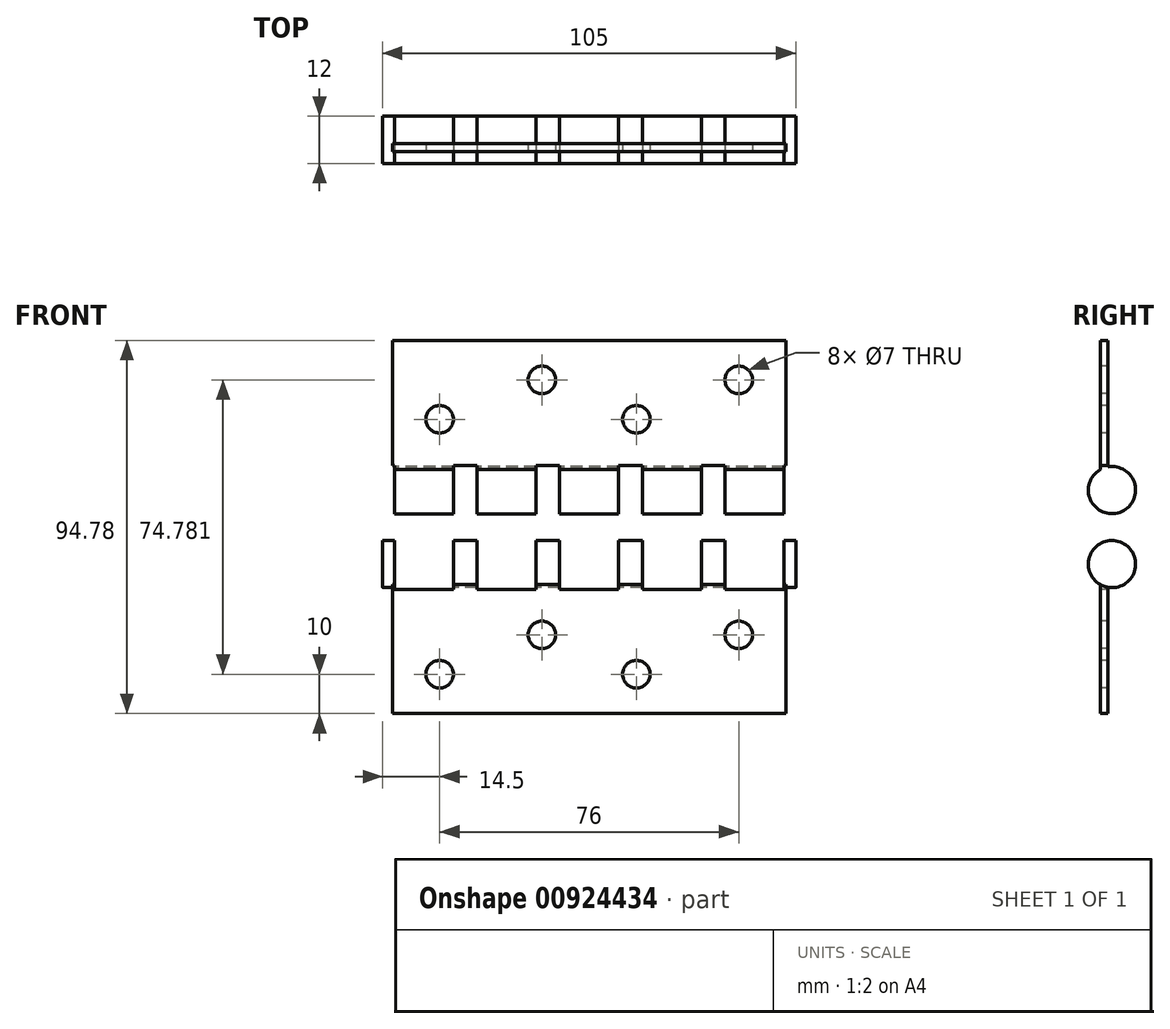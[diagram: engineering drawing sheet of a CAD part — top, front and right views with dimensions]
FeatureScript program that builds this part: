
annotation { "Feature Type Name" : "Feature", "Feature Type Description" : "" }
export const myFeature = defineFeature(function(context is Context, id is Id, definition is map)
    precondition{}
    {
        {
            var Q0;
            Q0=qCreatedBy(makeId("Right.planeOp"),FACE);
            var sketch = newSketch(context, id + "F0", { "sketchPlane" : qUnion([Q0])});
            skArc(sketch, "E0", {"start": v(-1, 32.08) * mm, "mid": v(2.03, 43.65) * mm, "end": v(-3, 32.8) * mm});
            skLineSegment(sketch, "E1", {"start": v(-1, 32.08) * mm, "end": v(-1, 0) * mm});
            skLineSegment(sketch, "E2", {"start": v(-1, 0) * mm, "end": v(-3, 0) * mm});
            skLineSegment(sketch, "E3", {"start": v(-3, 0) * mm, "end": v(-3, 32.8) * mm});
            skSolve(sketch);
        }
        {
            var Q0;
            Q0 = qSketchRegion(id + "F0", true);
            extrude(context, id + "F1", {"entities" : qUnion([Q0]), "depth" : 100 * mm, "offsetDistance" : 25 * mm});
        }
        {
            var Q0;
            Q0=makeQuery(id+"F1.opExtrude","CAP_FACE",FACE,{"disambiguationData":[OSD([sQuery(id+"F0.wireOp",EDGE,"NNvxePe8-nNrL-2dZQ-cABt-9JlAzgXYuufM.bottom"),sQuery(id+"F0.wireOp",EDGE,"NNvxePe8-nNrL-2dZQ-cABt-9JlAzgXYuufM.left"),sQuery(id+"F0.wireOp",EDGE,"NNvxePe8-nNrL-2dZQ-cABt-9JlAzgXYuufM.right"),sQuery(id+"F0.wireOp",EDGE,"E0")])],"isStart":false});
            var sketch = newSketch(context, id + "F2", { "sketchPlane" : qUnion([Q0])});
            skCircle(sketch, "E4", {"center": v(0, 38) * mm, "radius": 6 * mm});
            skSolve(sketch);
        }
        {
            var Q0;
            Q0 = qSketchRegion(id + "F2", true);
            extrude(context, id + "F3", {"entities" : qUnion([Q0]), "operationType" : NewBodyOperationType.ADD, "depth" : 2.5 * mm, "offsetDistance" : 25 * mm});
        }
        {
            var Q0;
            Q0=makeQuery(id+"F1.opExtrude","CAP_FACE",FACE,{"disambiguationData":[OSD([sQuery(id+"F0.wireOp",EDGE,"NNvxePe8-nNrL-2dZQ-cABt-9JlAzgXYuufM.bottom"),sQuery(id+"F0.wireOp",EDGE,"NNvxePe8-nNrL-2dZQ-cABt-9JlAzgXYuufM.left"),sQuery(id+"F0.wireOp",EDGE,"NNvxePe8-nNrL-2dZQ-cABt-9JlAzgXYuufM.right"),sQuery(id+"F0.wireOp",EDGE,"E0")])],"isStart":true});
            var sketch = newSketch(context, id + "F4", { "sketchPlane" : qUnion([Q0])});
            skCircle(sketch, "E5", {"center": v(0, 38) * mm, "radius": 6 * mm});
            skSolve(sketch);
        }
        {
            var Q0;
            Q0 = qSketchRegion(id + "F4", true);
            extrude(context, id + "F5", {"entities" : qUnion([Q0]), "operationType" : NewBodyOperationType.ADD, "depth" : 2.5 * mm, "offsetDistance" : 25 * mm});
        }
        {
            var Q0;
            Q0=makeQuery(id+"F1.opExtrude","CAP_FACE",FACE,{"disambiguationData":[OSD([sQuery(id+"F0.wireOp",EDGE,"NNvxePe8-nNrL-2dZQ-cABt-9JlAzgXYuufM.bottom"),sQuery(id+"F0.wireOp",EDGE,"NNvxePe8-nNrL-2dZQ-cABt-9JlAzgXYuufM.left"),sQuery(id+"F0.wireOp",EDGE,"NNvxePe8-nNrL-2dZQ-cABt-9JlAzgXYuufM.right"),sQuery(id+"F0.wireOp",EDGE,"E0")])],"isStart":true});
            var sketch = newSketch(context, id + "F6", { "sketchPlane" : qUnion([Q0])});
            skLineSegment(sketch, "E6.bottom", {"start": v(1, 94.78) * mm, "end": v(3, 94.78) * mm});
            skLineSegment(sketch, "E6.left", {"start": v(1, 94.78) * mm, "end": v(1, 62.7) * mm});
            skLineSegment(sketch, "E6.right", {"start": v(3, 94.78) * mm, "end": v(3, 61.98) * mm});
            skArc(sketch, "E7", {"start": v(1, 62.7) * mm, "mid": v(-2.03, 51.14) * mm, "end": v(3, 61.98) * mm});
            skSolve(sketch);
        }
        {
            var Q0;
            Q0=makeQuery(id+"F6.imprint","IMPRINT",FACE,{"disambiguationData":[TD([[makeQuery(id+"F6.imprint","IMPRINT",EDGE,{"derivedFrom":sQuery(id+"F6.wireOp",EDGE,"E6.bottom")}),-1.0]])]});
            extrude(context, id + "F7", {"entities" : qUnion([Q0]), "oppositeDirection" : true, "depth" : 100 * mm, "offsetDistance" : 25 * mm});
        }
        {
            var Q0;
            Q0=makeQuery(id+"F1.opExtrude","SWEPT_FACE",FACE,{"disambiguationData":[OSD([sQuery(id+"F0.wireOp",EDGE,"E3")])]});
            var sketch = newSketch(context, id + "F8", { "sketchPlane" : qUnion([Q0])});
            skLineSegment(sketch, "E8.bottom", {"start": v(0.5, 46.58) * mm, "end": v(15.5, 46.58) * mm});
            skLineSegment(sketch, "E8.top", {"start": v(0, 31.58) * mm, "end": v(15.5, 31.58) * mm});
            skLineSegment(sketch, "E8.left", {"start": v(0.5, 46.58) * mm, "end": v(0.5, 31.58) * mm});
            skLineSegment(sketch, "E8.right", {"start": v(15.5, 46.58) * mm, "end": v(15.5, 31.58) * mm});
            skLineSegment(sketch, "E9.1.0.0", {"start": v(36.5, 46.58) * mm, "end": v(36.5, 31.58) * mm});
            skLineSegment(sketch, "E9.1.0.1", {"start": v(21, 31.58) * mm, "end": v(36.5, 31.58) * mm});
            skLineSegment(sketch, "E9.1.0.2", {"start": v(21.5, 46.58) * mm, "end": v(36.5, 46.58) * mm});
            skLineSegment(sketch, "E9.1.0.3", {"start": v(21.5, 46.58) * mm, "end": v(21.5, 31.58) * mm});
            skLineSegment(sketch, "E9.2.0.0", {"start": v(57.5, 46.58) * mm, "end": v(57.5, 31.58) * mm});
            skLineSegment(sketch, "E9.2.0.1", {"start": v(42, 31.58) * mm, "end": v(57.5, 31.58) * mm});
            skLineSegment(sketch, "E9.2.0.2", {"start": v(42.5, 46.58) * mm, "end": v(57.5, 46.58) * mm});
            skLineSegment(sketch, "E9.2.0.3", {"start": v(42.5, 46.58) * mm, "end": v(42.5, 31.58) * mm});
            skLineSegment(sketch, "E9.3.0.0", {"start": v(78.5, 46.58) * mm, "end": v(78.5, 31.58) * mm});
            skLineSegment(sketch, "E9.3.0.1", {"start": v(63, 31.58) * mm, "end": v(78.5, 31.58) * mm});
            skLineSegment(sketch, "E9.3.0.2", {"start": v(63.5, 46.58) * mm, "end": v(78.5, 46.58) * mm});
            skLineSegment(sketch, "E9.3.0.3", {"start": v(63.5, 46.58) * mm, "end": v(63.5, 31.58) * mm});
            skLineSegment(sketch, "E9.4.0.0", {"start": v(99.5, 46.58) * mm, "end": v(99.5, 31.58) * mm});
            skLineSegment(sketch, "E9.4.0.1", {"start": v(84, 31.58) * mm, "end": v(99.5, 31.58) * mm});
            skLineSegment(sketch, "E9.4.0.2", {"start": v(84.5, 46.58) * mm, "end": v(99.5, 46.58) * mm});
            skLineSegment(sketch, "E9.4.0.3", {"start": v(84.5, 46.58) * mm, "end": v(84.5, 31.58) * mm});
            skLineSegment(sketch, "E9.direction1", {"start": v(0, 31.58) * mm, "end": v(21, 31.58) * mm, "construction": true});
            skSolve(sketch);
        }
        {
            var Q0;
            Q0 = qSketchRegion(id + "F8", true);
            extrude(context, id + "F9", {"entities" : qUnion([Q0]), "operationType" : NewBodyOperationType.REMOVE, "oppositeDirection" : true, "depth" : 25 * mm, "offsetDistance" : 25 * mm, "hasSecondDirection" : true, "secondDirectionOppositeDirection" : false, "secondDirectionDepth" : 25 * mm});
        }
        {
            var Q0;
            Q0=makeQuery(id+"F7.opExtrude","SWEPT_FACE",FACE,{"disambiguationData":[OSD([sQuery(id+"F6.wireOp",EDGE,"E6.right")])]});
            var sketch = newSketch(context, id + "F10", { "sketchPlane" : qUnion([Q0])});
            skLineSegment(sketch, "E10.bottom", {"start": v(-5.5, 62.98) * mm, "end": v(0.5, 62.98) * mm});
            skLineSegment(sketch, "E10.top", {"start": v(-5.5, 46.98) * mm, "end": v(0.5, 46.98) * mm});
            skLineSegment(sketch, "E10.left", {"start": v(-5.5, 62.98) * mm, "end": v(-5.5, 46.98) * mm});
            skLineSegment(sketch, "E10.right", {"start": v(0.5, 62.98) * mm, "end": v(0.5, 46.98) * mm});
            skLineSegment(sketch, "E11.1.0.0", {"start": v(15.5, 46.98) * mm, "end": v(21.5, 46.98) * mm});
            skLineSegment(sketch, "E11.1.0.1", {"start": v(21.5, 62.98) * mm, "end": v(21.5, 46.98) * mm});
            skLineSegment(sketch, "E11.1.0.2", {"start": v(15.5, 62.98) * mm, "end": v(15.5, 46.98) * mm});
            skLineSegment(sketch, "E11.1.0.3", {"start": v(15.5, 62.98) * mm, "end": v(21.5, 62.98) * mm});
            skLineSegment(sketch, "E11.2.0.0", {"start": v(36.5, 46.98) * mm, "end": v(42.5, 46.98) * mm});
            skLineSegment(sketch, "E11.2.0.1", {"start": v(42.5, 62.98) * mm, "end": v(42.5, 46.98) * mm});
            skLineSegment(sketch, "E11.2.0.2", {"start": v(36.5, 62.98) * mm, "end": v(36.5, 46.98) * mm});
            skLineSegment(sketch, "E11.2.0.3", {"start": v(36.5, 62.98) * mm, "end": v(42.5, 62.98) * mm});
            skLineSegment(sketch, "E11.3.0.0", {"start": v(57.5, 46.98) * mm, "end": v(63.5, 46.98) * mm});
            skLineSegment(sketch, "E11.3.0.1", {"start": v(63.5, 62.98) * mm, "end": v(63.5, 46.98) * mm});
            skLineSegment(sketch, "E11.3.0.2", {"start": v(57.5, 62.98) * mm, "end": v(57.5, 46.98) * mm});
            skLineSegment(sketch, "E11.3.0.3", {"start": v(57.5, 62.98) * mm, "end": v(63.5, 62.98) * mm});
            skLineSegment(sketch, "E11.4.0.0", {"start": v(78.5, 46.98) * mm, "end": v(84.5, 46.98) * mm});
            skLineSegment(sketch, "E11.4.0.1", {"start": v(84.5, 62.98) * mm, "end": v(84.5, 46.98) * mm});
            skLineSegment(sketch, "E11.4.0.2", {"start": v(78.5, 62.98) * mm, "end": v(78.5, 46.98) * mm});
            skLineSegment(sketch, "E11.4.0.3", {"start": v(78.5, 62.98) * mm, "end": v(84.5, 62.98) * mm});
            skLineSegment(sketch, "E11.5.0.0", {"start": v(99.5, 46.98) * mm, "end": v(105.5, 46.98) * mm});
            skLineSegment(sketch, "E11.5.0.1", {"start": v(105.5, 62.98) * mm, "end": v(105.5, 46.98) * mm});
            skLineSegment(sketch, "E11.5.0.2", {"start": v(99.5, 62.98) * mm, "end": v(99.5, 46.98) * mm});
            skLineSegment(sketch, "E11.5.0.3", {"start": v(99.5, 62.98) * mm, "end": v(105.5, 62.98) * mm});
            skLineSegment(sketch, "E11.direction1", {"start": v(-5.5, 46.98) * mm, "end": v(15.5, 46.98) * mm, "construction": true});
            skSolve(sketch);
        }
        {
            var Q0;
            Q0 = qSketchRegion(id + "F10", true);
            extrude(context, id + "F11", {"entities" : qUnion([Q0]), "operationType" : NewBodyOperationType.REMOVE, "oppositeDirection" : true, "depth" : 25 * mm, "offsetDistance" : 25 * mm, "hasSecondDirection" : true, "secondDirectionOppositeDirection" : false, "secondDirectionDepth" : 25 * mm});
        }
        {
            var Q0;
            Q0=makeQuery(id+"F1.opExtrude","SWEPT_FACE",FACE,{"disambiguationData":[OSD([sQuery(id+"F0.wireOp",EDGE,"E3")])]});
            var sketch = newSketch(context, id + "F12", { "sketchPlane" : qUnion([Q0])});
            skPoint(sketch, "E12", {"position": v(12, 10) * mm});
            skPoint(sketch, "E13", {"position": v(38, 20) * mm});
            skPoint(sketch, "E14", {"position": v(62, 10) * mm});
            skPoint(sketch, "E15", {"position": v(88, 20) * mm});
            skSolve(sketch);
        }
        {
            var Q0;
            Q0=sQuery(id+"F12.wireOp",VERTEX,"E12");
            var Q1;
            Q1=sQuery(id+"F12.wireOp",VERTEX,"E13");
            var Q2;
            Q2=sQuery(id+"F12.wireOp",VERTEX,"E14");
            var Q3;
            Q3=sQuery(id+"F12.wireOp",VERTEX,"E15");
            var Q4;
            Q4=makeQuery(id+"F1.opExtrude","SWEPT_BODY",BODY,{"disambiguationData":[OSD([sQuery(id+"F0.wireOp",EDGE,"E0"),sQuery(id+"F0.wireOp",EDGE,"E1"),sQuery(id+"F0.wireOp",EDGE,"E2"),sQuery(id+"F0.wireOp",EDGE,"E3")])]});
            hole(context, id + "F13", {"style" : HoleStyle.SIMPLE, "endStyle" : HoleEndStyle.THROUGH, "standardTappedOrClearance" : lookupTablePath({ "standard" : "ISO", "size" : "7", "type" : "Drilled" }), "standardBlindInLast" : lookupTablePath({ "standard" : "ISO", "size" : "7", "type" : "Drilled" }), "holeDiameter" : 7 * mm, "majorDiameter" : 10 * mm, "isTappedThrough" : true, "tappedDepth" : 12 * mm, "tapClearance" : 3, "locations" : qUnion([Q0, Q1, Q2, Q3]), "scope" : qUnion([Q4])});
        }
        {
            var Q0;
            Q0=makeQuery(id+"F7.opExtrude","SWEPT_FACE",FACE,{"disambiguationData":[OSD([sQuery(id+"F6.wireOp",EDGE,"E6.right")])]});
            var sketch = newSketch(context, id + "F14", { "sketchPlane" : qUnion([Q0])});
            skPoint(sketch, "E16", {"position": v(12, 74.78) * mm});
            skPoint(sketch, "E17", {"position": v(38, 84.78) * mm});
            skPoint(sketch, "E18", {"position": v(62, 74.78) * mm});
            skPoint(sketch, "E19", {"position": v(88, 84.78) * mm});
            skSolve(sketch);
        }
        {
            var Q0;
            Q0=sQuery(id+"F14.wireOp",VERTEX,"E16");
            var Q1;
            Q1=sQuery(id+"F14.wireOp",VERTEX,"E17");
            var Q2;
            Q2=sQuery(id+"F14.wireOp",VERTEX,"E18");
            var Q3;
            Q3=sQuery(id+"F14.wireOp",VERTEX,"E19");
            var Q4;
            Q4=makeQuery(id+"F7.opExtrude","SWEPT_BODY",BODY,{"disambiguationData":[OSD([sQuery(id+"F6.wireOp",EDGE,"E6.bottom"),sQuery(id+"F6.wireOp",EDGE,"E6.left"),sQuery(id+"F6.wireOp",EDGE,"E6.right"),sQuery(id+"F6.wireOp",EDGE,"E7")])]});
            hole(context, id + "F15", {"style" : HoleStyle.SIMPLE, "endStyle" : HoleEndStyle.THROUGH, "standardTappedOrClearance" : lookupTablePath({ "standard" : "ISO", "size" : "7", "type" : "Drilled" }), "standardBlindInLast" : lookupTablePath({ "standard" : "ISO", "size" : "7", "type" : "Drilled" }), "holeDiameter" : 7 * mm, "majorDiameter" : 5 * mm, "isTappedThrough" : true, "tappedDepth" : 12 * mm, "tapClearance" : 3, "locations" : qUnion([Q0, Q1, Q2, Q3]), "scope" : qUnion([Q4])});
        }
    });
